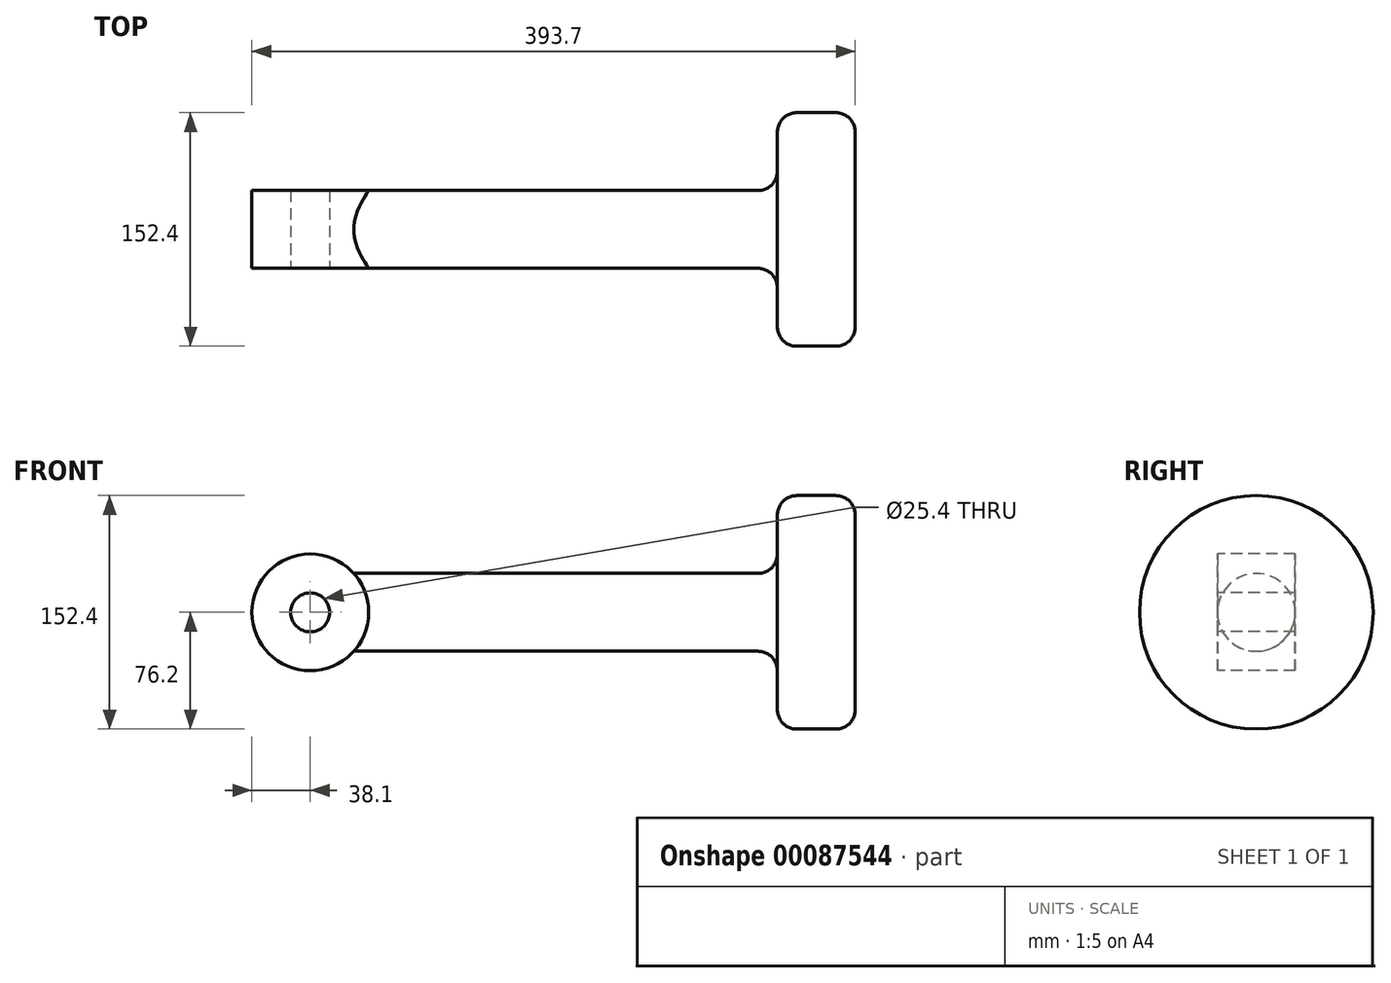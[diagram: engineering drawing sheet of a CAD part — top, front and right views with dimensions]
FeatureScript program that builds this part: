
annotation { "Feature Type Name" : "Feature", "Feature Type Description" : "" }
export const myFeature = defineFeature(function(context is Context, id is Id, definition is map)
    precondition{}
    {
        {
            var Q0;
            Q0=qCreatedBy(makeId("Front.planeOp"),FACE);
            var sketch = newSketch(context, id + "F0", { "sketchPlane" : qUnion([Q0])});
            skLineSegment(sketch, "E0", {"start": v(0, 0) * mm, "end": v(-355.6, 0) * mm});
            skLineSegment(sketch, "E1", {"start": v(-355.6, 0) * mm, "end": v(-355.6, 25.4) * mm});
            skLineSegment(sketch, "E2", {"start": v(-355.6, 25.4) * mm, "end": v(-50.8, 25.4) * mm});
            skLineSegment(sketch, "E3", {"start": v(-50.8, 25.4) * mm, "end": v(-50.8, 76.2) * mm});
            skLineSegment(sketch, "E4", {"start": v(-50.8, 76.2) * mm, "end": v(0, 76.2) * mm});
            skLineSegment(sketch, "E5", {"start": v(0, 76.2) * mm, "end": v(0, 0) * mm});
            skSolve(sketch);
        }
        {
            var Q0;
            Q0=makeQuery(id+"F0.imprint","IMPRINT",FACE,{"disambiguationData":[TD([[makeQuery(id+"F0.imprint","IMPRINT",EDGE,{"derivedFrom":sQuery(id+"F0.wireOp",EDGE,"E0")}),-1.0]])]});
            var Q1;
            Q1=sQuery(id+"F0.wireOp",EDGE,"E0");
            revolve(context, id + "F1", {"entities" : qUnion([Q0]), "axis" : qUnion([Q1]), "revolveType" : RevolveType.FULL});
        }
        {
            var Q0;
            Q0=makeQuery(id+"F1.opRevolve","SWEPT_FACE",FACE,{"disambiguationData":[OSD([sQuery(id+"F0.wireOp",EDGE,"E1")])]});
            var sketch = newSketch(context, id + "F2", { "sketchPlane" : qUnion([Q0])});
            skLineSegment(sketch, "E6", {"start": v(0, 0) * mm, "end": v(-25.4, 0) * mm, "construction": true});
            skLineSegment(sketch, "E7", {"start": v(-25.4, 0) * mm, "end": v(-25.4, 12.7) * mm, "construction": true});
            skLineSegment(sketch, "E8", {"start": v(-25.4, 12.7) * mm, "end": v(25.4, 12.7) * mm});
            skLineSegment(sketch, "E9", {"start": v(25.4, 12.7) * mm, "end": v(25.4, 38.1) * mm});
            skLineSegment(sketch, "E10", {"start": v(25.4, 38.1) * mm, "end": v(-25.4, 38.1) * mm});
            skLineSegment(sketch, "E11", {"start": v(-25.4, 38.1) * mm, "end": v(-25.4, 12.7) * mm});
            skLineSegment(sketch, "E12", {"start": v(25.4, 12.7) * mm, "end": v(25.4, 0) * mm, "construction": true});
            skSolve(sketch);
        }
        {
            var Q0;
            Q0 = qSketchRegion(id + "F2", true);
            var Q1;
            Q1=sQuery(id+"F2.wireOp",EDGE,"E6");
            revolve(context, id + "F3", {"operationType" : NewBodyOperationType.ADD, "entities" : qUnion([Q0]), "axis" : qUnion([Q1]), "revolveType" : RevolveType.FULL});
        }
        {
            var Q0;
            Q0=makeQuery(id+"F3.opRevolve","SWEPT_FACE",FACE,{"disambiguationData":[OSD([sQuery(id+"F2.wireOp",EDGE,"E11")])]});
            var sketch = newSketch(context, id + "F4", { "sketchPlane" : qUnion([Q0])});
            skCircle(sketch, "E13", {"center": v(355.6, 0) * mm, "radius": 12.7 * mm});
            skSolve(sketch);
        }
        {
            var Q0;
            Q0=makeQuery(id+"F4.imprint","IMPRINT",FACE,{"disambiguationData":[TD([[makeQuery(id+"F4.imprint","IMPRINT",EDGE,{"derivedFrom":sQuery(id+"F4.wireOp",EDGE,"E13")}),-1.0]])]});
            extrude(context, id + "F5", {"entities" : qUnion([Q0]), "operationType" : NewBodyOperationType.REMOVE, "oppositeDirection" : true, "depth" : 105.95 * mm});
        }
        {
            var Q0;
            Q0=makeQuery(id+"F1.opRevolve","SWEPT_FACE",FACE,{"disambiguationData":[OSD([sQuery(id+"F0.wireOp",EDGE,"E5")])]});
            var Q1;
            Q1=makeQuery(id+"F1.opRevolve","SWEPT_FACE",FACE,{"disambiguationData":[OSD([sQuery(id+"F0.wireOp",EDGE,"E3")])]});
            fillet(context, id + "F6", {"entities" : qUnion([Q0, Q1]), "radius" : 12.7 * mm, "tangentPropagation" : true, "allowEdgeOverflow" : false});
        }
    });
